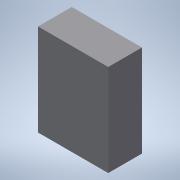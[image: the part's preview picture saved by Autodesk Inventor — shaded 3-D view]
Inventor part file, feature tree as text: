
AUTODESK INVENTOR PART (.ipt)
format: ipt  version: 2020 (Build 240168000, 168)  size: 87,552 bytes
history: native  units: mm
features: other x1, extrude x1, sketch x1
ambient origin geometry x8: Origin, YZ Plane, XZ Plane, XY Plane, X Axis, Y Axis, Z Axis, Center Point
bodies: Body1 (feature_tree)
feature tree (3):
  other  "Bryła1"
  extrude  "Wyciągnięcie proste1"  Depth=52.0mm
  sketch  "Szkic1"
